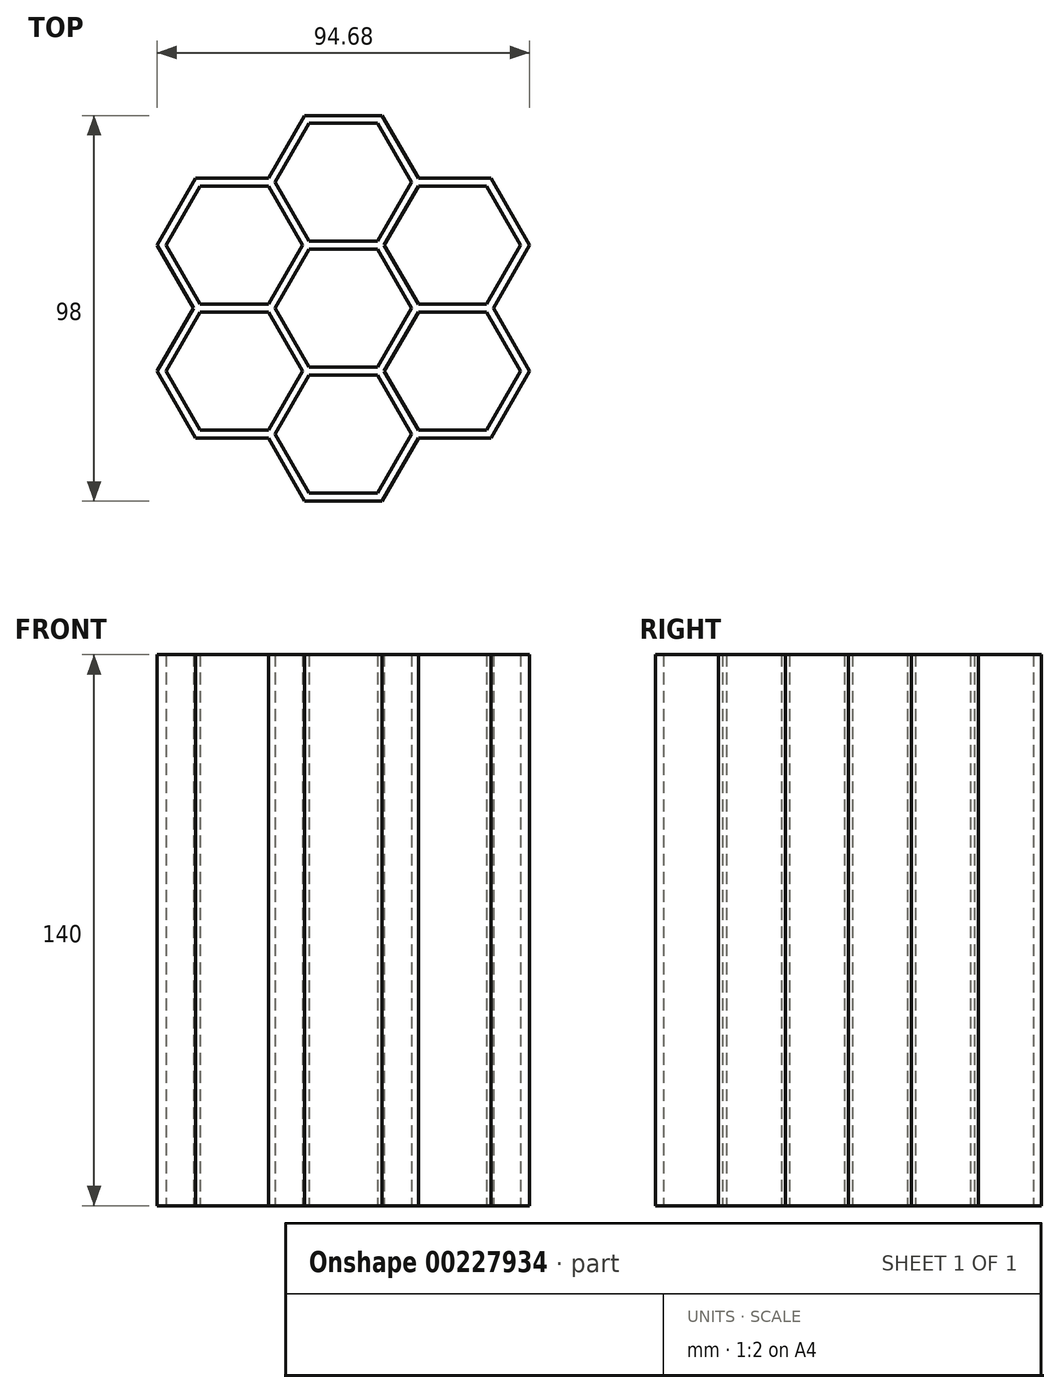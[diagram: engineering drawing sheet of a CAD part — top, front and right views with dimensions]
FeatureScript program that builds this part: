
annotation { "Feature Type Name" : "Feature", "Feature Type Description" : "" }
export const myFeature = defineFeature(function(context is Context, id is Id, definition is map)
    precondition{}
    {
        {
            var Q0;
            Q0=qCreatedBy(makeId("Top.planeOp"),FACE);
            var sketch = newSketch(context, id + "F0", { "sketchPlane" : qUnion([Q0])});
            skCircle(sketch, "E0.cCircle", {"center": v(0, 0) * mm, "radius": 17 * mm, "construction": true});
            skLineSegment(sketch, "E0.0", {"start": v(-8.66, 17) * mm, "end": v(8.66, 17) * mm});
            skLineSegment(sketch, "E0.1", {"start": v(10.4, 16) * mm, "end": v(19.05, 1) * mm});
            skLineSegment(sketch, "E0.2", {"start": v(19.05, -1) * mm, "end": v(9.81, -17) * mm});
            skLineSegment(sketch, "E0.3", {"start": v(9.81, -17) * mm, "end": v(-9.81, -17) * mm});
            skLineSegment(sketch, "E0.4", {"start": v(-9.81, -17) * mm, "end": v(-19.05, -1) * mm});
            skLineSegment(sketch, "E0.5", {"start": v(-19.05, 1) * mm, "end": v(-10.4, 16) * mm});
            skPoint(sketch, "E0.0.midPoint", {"position": v(0, 17) * mm});
            skCircle(sketch, "E1.cCircle", {"center": v(0, 0) * mm, "radius": 15 * mm, "construction": true});
            skLineSegment(sketch, "E1.0", {"start": v(-8.66, 15) * mm, "end": v(8.66, 15) * mm});
            skLineSegment(sketch, "E1.1", {"start": v(8.66, 15) * mm, "end": v(17.32, 0) * mm});
            skLineSegment(sketch, "E1.2", {"start": v(17.32, 0) * mm, "end": v(8.66, -15) * mm});
            skLineSegment(sketch, "E1.3", {"start": v(8.66, -15) * mm, "end": v(-8.66, -15) * mm});
            skLineSegment(sketch, "E1.4", {"start": v(-8.66, -15) * mm, "end": v(-17.32, 0) * mm});
            skLineSegment(sketch, "E1.5", {"start": v(-17.32, 0) * mm, "end": v(-8.66, 15) * mm});
            skPoint(sketch, "E1.0.midPoint", {"position": v(0, 15) * mm});
            skLineSegment(sketch, "E2.0.1.0", {"start": v(-17.32, 32) * mm, "end": v(-8.66, 47) * mm});
            skPoint(sketch, "E2.0.1.1", {"position": v(0, 49) * mm});
            skPoint(sketch, "E2.0.1.2", {"position": v(0, 47) * mm});
            skLineSegment(sketch, "E2.0.1.3", {"start": v(-8.66, 17) * mm, "end": v(-17.32, 32) * mm});
            skLineSegment(sketch, "E2.0.1.4", {"start": v(8.66, 17) * mm, "end": v(-8.66, 17) * mm});
            skLineSegment(sketch, "E2.0.1.5", {"start": v(17.32, 32) * mm, "end": v(8.66, 17) * mm});
            skLineSegment(sketch, "E2.0.1.6", {"start": v(8.66, 47) * mm, "end": v(17.32, 32) * mm});
            skLineSegment(sketch, "E2.0.1.7", {"start": v(-8.66, 47) * mm, "end": v(8.66, 47) * mm});
            skCircle(sketch, "E2.0.1.8", {"center": v(0, 32) * mm, "radius": 15 * mm, "construction": true});
            skLineSegment(sketch, "E2.0.1.9", {"start": v(-19.05, 33) * mm, "end": v(-10.4, 48) * mm});
            skLineSegment(sketch, "E2.0.1.10", {"start": v(-10.4, 16) * mm, "end": v(-19.05, 31) * mm});
            skLineSegment(sketch, "E2.0.1.11", {"start": v(8.66, 15) * mm, "end": v(-8.66, 15) * mm});
            skLineSegment(sketch, "E2.0.1.12", {"start": v(14.72, 23.5) * mm, "end": v(10.4, 16) * mm});
            skLineSegment(sketch, "E2.0.1.13", {"start": v(10.4, 48) * mm, "end": v(19.05, 33) * mm});
            skLineSegment(sketch, "E2.0.1.14", {"start": v(-8.66, 49) * mm, "end": v(8.66, 49) * mm});
            skCircle(sketch, "E2.0.1.15", {"center": v(0, 32) * mm, "radius": 17 * mm, "construction": true});
            skLineSegment(sketch, "E2.0.2.0", {"start": v(-17.32, 64) * mm, "end": v(-8.66, 79) * mm});
            skPoint(sketch, "E2.0.2.1", {"position": v(0, 81) * mm});
            skPoint(sketch, "E2.0.2.2", {"position": v(0, 79) * mm});
            skLineSegment(sketch, "E2.0.2.3", {"start": v(-8.66, 49) * mm, "end": v(-17.32, 64) * mm});
            skLineSegment(sketch, "E2.0.2.4", {"start": v(8.66, 49) * mm, "end": v(-8.66, 49) * mm});
            skLineSegment(sketch, "E2.0.2.5", {"start": v(17.32, 64) * mm, "end": v(8.66, 49) * mm});
            skLineSegment(sketch, "E2.0.2.6", {"start": v(8.66, 79) * mm, "end": v(17.32, 64) * mm});
            skLineSegment(sketch, "E2.0.2.7", {"start": v(-8.66, 79) * mm, "end": v(8.66, 79) * mm});
            skCircle(sketch, "E2.0.2.8", {"center": v(0, 64) * mm, "radius": 15 * mm, "construction": true});
            skLineSegment(sketch, "E2.0.2.9", {"start": v(-19.05, 65) * mm, "end": v(-9.81, 81) * mm});
            skLineSegment(sketch, "E2.0.2.10", {"start": v(-10.4, 48) * mm, "end": v(-19.05, 63) * mm});
            skLineSegment(sketch, "E2.0.2.11", {"start": v(8.66, 47) * mm, "end": v(-8.66, 47) * mm});
            skLineSegment(sketch, "E2.0.2.12", {"start": v(19.05, 63) * mm, "end": v(10.4, 48) * mm});
            skLineSegment(sketch, "E2.0.2.13", {"start": v(9.81, 81) * mm, "end": v(19.05, 65) * mm});
            skLineSegment(sketch, "E2.0.2.14", {"start": v(-9.81, 81) * mm, "end": v(9.81, 81) * mm});
            skCircle(sketch, "E2.0.2.15", {"center": v(0, 64) * mm, "radius": 17 * mm, "construction": true});
            skLineSegment(sketch, "E2.direction1", {"start": v(-9.81, -17) * mm, "end": v(16.34, -17) * mm, "construction": true});
            skLineSegment(sketch, "E2.direction2", {"start": v(-9.81, -17) * mm, "end": v(-9.81, 15) * mm, "construction": true});
            skCircle(sketch, "E3.cCircle", {"center": v(27.71, 16) * mm, "radius": 17 * mm, "construction": true});
            skLineSegment(sketch, "E3.0", {"start": v(19.05, 33) * mm, "end": v(36.37, 33) * mm});
            skLineSegment(sketch, "E3.1", {"start": v(38.1, 32) * mm, "end": v(47.34, 16) * mm});
            skLineSegment(sketch, "E3.2", {"start": v(47.34, 16) * mm, "end": v(37.53, -1) * mm});
            skLineSegment(sketch, "E3.3", {"start": v(37.53, -1) * mm, "end": v(19.05, -1) * mm});
            skLineSegment(sketch, "E3.4", {"start": v(17.32, 0) * mm, "end": v(8.66, 15) * mm});
            skLineSegment(sketch, "E3.5", {"start": v(8.66, 17) * mm, "end": v(17.32, 32) * mm});
            skPoint(sketch, "E3.0.midPoint", {"position": v(27.71, 33) * mm});
            skCircle(sketch, "E4.cCircle", {"center": v(27.71, 16) * mm, "radius": 15 * mm, "construction": true});
            skLineSegment(sketch, "E4.0", {"start": v(19.05, 31) * mm, "end": v(36.37, 31) * mm});
            skLineSegment(sketch, "E4.1", {"start": v(36.37, 31) * mm, "end": v(45.03, 16) * mm});
            skLineSegment(sketch, "E4.2", {"start": v(45.03, 16) * mm, "end": v(36.37, 1) * mm});
            skLineSegment(sketch, "E4.3", {"start": v(36.37, 1) * mm, "end": v(19.05, 1) * mm});
            skLineSegment(sketch, "E4.4", {"start": v(19.05, 1) * mm, "end": v(10.4, 16) * mm});
            skLineSegment(sketch, "E4.5", {"start": v(10.4, 16) * mm, "end": v(19.05, 31) * mm});
            skPoint(sketch, "E4.0.midPoint", {"position": v(27.71, 31) * mm});
            skPoint(sketch, "E5.orphan", {"position": v(-9.81, 17) * mm});
            skPoint(sketch, "E6.orphan", {"position": v(9.81, 17) * mm});
            skPoint(sketch, "E7.orphan", {"position": v(9.81, 15) * mm});
            skPoint(sketch, "E8.orphan", {"position": v(-9.81, 49) * mm});
            skPoint(sketch, "E9.orphan", {"position": v(-9.81, 47) * mm});
            skPoint(sketch, "E10.orphan", {"position": v(9.81, 49) * mm});
            skPoint(sketch, "E11.orphan", {"position": v(9.81, 47) * mm});
            skPoint(sketch, "E12.0.1.0", {"position": v(27.71, 63) * mm});
            skCircle(sketch, "E12.0.1.1", {"center": v(27.71, 48) * mm, "radius": 15 * mm, "construction": true});
            skLineSegment(sketch, "E12.0.1.2", {"start": v(36.37, 33) * mm, "end": v(19.05, 33) * mm});
            skLineSegment(sketch, "E12.0.1.3", {"start": v(19.05, 65) * mm, "end": v(37.53, 65) * mm});
            skLineSegment(sketch, "E12.0.1.4", {"start": v(19.05, 63) * mm, "end": v(36.37, 63) * mm});
            skLineSegment(sketch, "E12.0.1.5", {"start": v(36.37, 31) * mm, "end": v(19.05, 31) * mm});
            skPoint(sketch, "E12.0.1.6", {"position": v(27.71, 65) * mm});
            skCircle(sketch, "E12.0.1.7", {"center": v(27.71, 48) * mm, "radius": 17 * mm, "construction": true});
            skLineSegment(sketch, "E12.0.1.8", {"start": v(36.37, 63) * mm, "end": v(45.03, 48) * mm});
            skLineSegment(sketch, "E12.0.1.9", {"start": v(37.53, 65) * mm, "end": v(47.34, 48) * mm});
            skLineSegment(sketch, "E12.0.1.10", {"start": v(47.34, 48) * mm, "end": v(38.1, 32) * mm});
            skLineSegment(sketch, "E12.0.1.11", {"start": v(45.03, 48) * mm, "end": v(36.37, 33) * mm});
            skLineSegment(sketch, "E12.0.1.12", {"start": v(8.66, 49) * mm, "end": v(17.32, 64) * mm});
            skLineSegment(sketch, "E12.0.1.13", {"start": v(17, 32.57) * mm, "end": v(8.66, 47) * mm});
            skLineSegment(sketch, "E12.direction1", {"start": v(17.9, -1) * mm, "end": v(42.9, -1) * mm, "construction": true});
            skLineSegment(sketch, "E12.direction2", {"start": v(17.9, -1) * mm, "end": v(17.9, 31) * mm, "construction": true});
            skPoint(sketch, "E13.orphan", {"position": v(17.9, 33) * mm});
            skPoint(sketch, "E14.orphan", {"position": v(19.63, 32) * mm});
            skPoint(sketch, "E15.orphan", {"position": v(37.53, 33) * mm});
            skPoint(sketch, "E16.orphan", {"position": v(37.53, 31) * mm});
            skPoint(sketch, "E17.orphan", {"position": v(19.63, 0) * mm});
            skPoint(sketch, "E18.orphan", {"position": v(8.08, 16) * mm});
            skPoint(sketch, "E19.orphan", {"position": v(8.08, 48) * mm});
            skPoint(sketch, "E20.orphan", {"position": v(19.63, 64) * mm});
            skPoint(sketch, "E21.orphan", {"position": v(17.9, 65) * mm});
            skCircle(sketch, "E22.cCircle", {"center": v(-27.71, 16) * mm, "radius": 17 * mm, "construction": true});
            skLineSegment(sketch, "E22.0", {"start": v(-36.37, 33) * mm, "end": v(-19.05, 33) * mm});
            skLineSegment(sketch, "E22.1", {"start": v(-17.32, 32) * mm, "end": v(-8.66, 17) * mm});
            skLineSegment(sketch, "E22.2", {"start": v(-8.66, 15) * mm, "end": v(-17.32, 0) * mm});
            skLineSegment(sketch, "E22.3", {"start": v(-19.05, -1) * mm, "end": v(-37.53, -1) * mm});
            skLineSegment(sketch, "E22.4", {"start": v(-37.53, -1) * mm, "end": v(-47.34, 16) * mm});
            skLineSegment(sketch, "E22.5", {"start": v(-47.34, 16) * mm, "end": v(-38.1, 32) * mm});
            skPoint(sketch, "E22.0.midPoint", {"position": v(-27.71, 33) * mm});
            skCircle(sketch, "E23.cCircle", {"center": v(-27.71, 16) * mm, "radius": 15 * mm, "construction": true});
            skLineSegment(sketch, "E23.0", {"start": v(-19.05, 1) * mm, "end": v(-36.37, 1) * mm});
            skLineSegment(sketch, "E23.1", {"start": v(-36.37, 1) * mm, "end": v(-45.03, 16) * mm});
            skLineSegment(sketch, "E23.2", {"start": v(-45.03, 16) * mm, "end": v(-36.37, 31) * mm});
            skLineSegment(sketch, "E23.3", {"start": v(-36.37, 31) * mm, "end": v(-19.05, 31) * mm});
            skLineSegment(sketch, "E23.4", {"start": v(-19.05, 31) * mm, "end": v(-10.4, 16) * mm});
            skLineSegment(sketch, "E23.5", {"start": v(-10.4, 16) * mm, "end": v(-19.05, 1) * mm});
            skPoint(sketch, "E23.0.midPoint", {"position": v(-27.71, 1) * mm});
            skLineSegment(sketch, "E24.0.1.0", {"start": v(-36.37, 63) * mm, "end": v(-19.05, 63) * mm});
            skLineSegment(sketch, "E24.0.1.1", {"start": v(-36.37, 33) * mm, "end": v(-45.03, 48) * mm});
            skLineSegment(sketch, "E24.0.1.2", {"start": v(-47.34, 48) * mm, "end": v(-37.53, 65) * mm});
            skLineSegment(sketch, "E24.0.1.3", {"start": v(-19.05, 33) * mm, "end": v(-36.37, 33) * mm});
            skLineSegment(sketch, "E24.0.1.5", {"start": v(-38.1, 32) * mm, "end": v(-47.34, 48) * mm});
            skLineSegment(sketch, "E24.0.1.6", {"start": v(-45.03, 48) * mm, "end": v(-36.37, 63) * mm});
            skPoint(sketch, "E24.0.1.7", {"position": v(-27.71, 65) * mm});
            skLineSegment(sketch, "E24.0.1.8", {"start": v(-19.05, 31) * mm, "end": v(-36.37, 31) * mm});
            skLineSegment(sketch, "E24.0.1.9", {"start": v(-37.53, 65) * mm, "end": v(-19.05, 65) * mm});
            skLineSegment(sketch, "E24.0.1.10", {"start": v(-17.32, 64) * mm, "end": v(-8.66, 49) * mm});
            skLineSegment(sketch, "E24.0.1.11", {"start": v(-9, 46.43) * mm, "end": v(-17.32, 32) * mm});
            skLineSegment(sketch, "E24.direction1", {"start": v(-37.53, -1) * mm, "end": v(-19.05, -1) * mm, "construction": true});
            skLineSegment(sketch, "E24.direction2", {"start": v(-37.53, -1) * mm, "end": v(-37.53, 31) * mm, "construction": true});
            skPoint(sketch, "E25.orphan", {"position": v(-17.9, 33) * mm});
            skPoint(sketch, "E26.orphan", {"position": v(-17.9, 31) * mm});
            skPoint(sketch, "E27.orphan", {"position": v(-37.53, 33) * mm});
            skPoint(sketch, "E28.orphan", {"position": v(-8.08, 16) * mm});
            skLineSegment(sketch, "E29.trimOffspring", {"start": v(-17.9, -1) * mm, "end": v(-12.53, -1) * mm, "construction": true});
            skPoint(sketch, "E30.orphan", {"position": v(-19.63, 0) * mm});
            skPoint(sketch, "E31.orphan", {"position": v(-19.63, 32) * mm});
            skPoint(sketch, "E32.orphan", {"position": v(-8.08, 48) * mm});
            skPoint(sketch, "E33.orphan", {"position": v(-17.9, 65) * mm});
            skPoint(sketch, "E34.orphan", {"position": v(-19.63, 64) * mm});
            skSolve(sketch);
        }
        {
            var Q0;
            Q0 = qSketchRegion(id + "F0", true);
            extrude(context, id + "F1", {"entities" : qUnion([Q0]), "depth" : 140 * mm});
        }
    });
